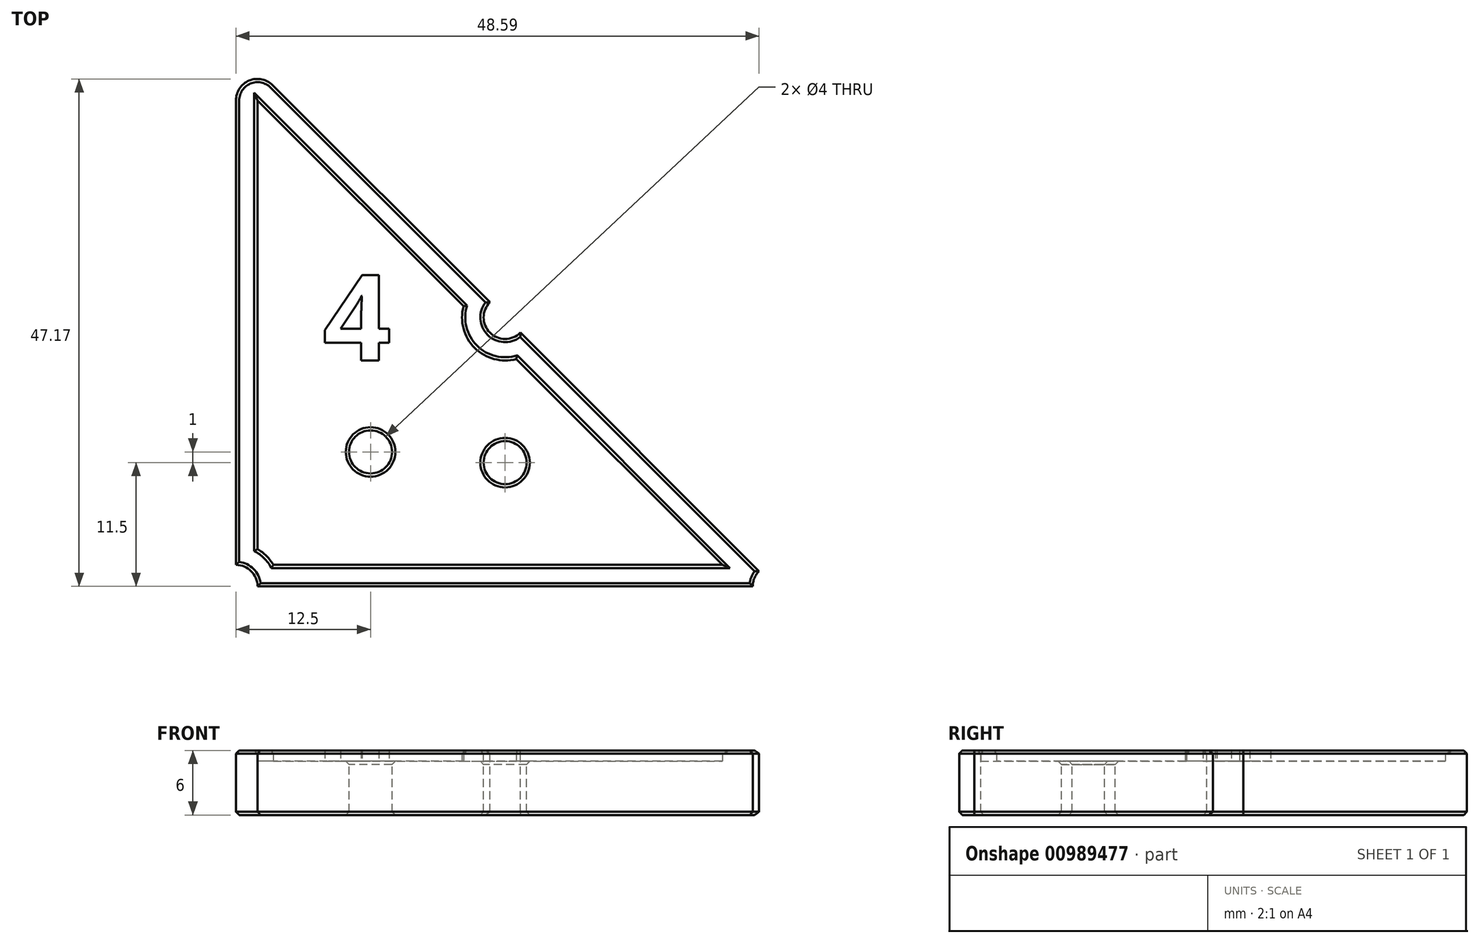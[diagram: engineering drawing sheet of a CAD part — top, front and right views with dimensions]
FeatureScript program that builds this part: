
annotation { "Feature Type Name" : "Feature", "Feature Type Description" : "" }
export const myFeature = defineFeature(function(context is Context, id is Id, definition is map)
    precondition{}
    {
        {
            var Q0;
            Q0=qCreatedBy(makeId("Top.planeOp"),FACE);
            var sketch = newSketch(context, id + "F0", { "sketchPlane" : qUnion([Q0])});
            skLineSegment(sketch, "E0", {"start": v(-25, 25) * mm, "end": v(-25, -25) * mm});
            skLineSegment(sketch, "E1", {"start": v(-25, -25) * mm, "end": v(25, -25) * mm});
            skLineSegment(sketch, "E2", {"start": v(25, -25) * mm, "end": v(-25, 25) * mm});
            skPoint(sketch, "E3", {"position": v(0, 0) * mm});
            skCircle(sketch, "E4", {"center": v(-25, -25) * mm, "radius": 2 * mm});
            skCircle(sketch, "E5", {"center": v(25, -25) * mm, "radius": 2 * mm});
            skCircle(sketch, "E6", {"center": v(0, 0) * mm, "radius": 2 * mm});
            skArc(sketch, "E7", {"start": v(-21.59, 21.59) * mm, "mid": v(-23.77, 22.02) * mm, "end": v(-25, 20.17) * mm});
            skCircle(sketch, "E8", {"center": v(-12.5, -12.5) * mm, "radius": 2 * mm});
            skLineSegment(sketch, "E9", {"start": v(0, 0) * mm, "end": v(-25, -25) * mm, "construction": true});
            skCircle(sketch, "E10", {"center": v(0, -13.5) * mm, "radius": 2 * mm});
            skLineSegment(sketch, "E11", {"start": v(0, -2) * mm, "end": v(0, -25) * mm, "construction": true});
            skPoint(sketch, "E11.startSnap0", {"position": v(0, -25) * mm});
            skLineSegment(sketch, "E12", {"start": v(-2, 2) * mm, "end": v(-2, -7.39) * mm, "construction": true});
            skLineSegment(sketch, "E13", {"start": v(-2, 0) * mm, "end": v(-25, 0) * mm, "construction": true});
            skText(sketch, "E14", { "text": "4", "fontName": "OpenSans-Bold.ttf"});
            skPoint(sketch, "E15", {"position": v(-13.5, 0) * mm});
            const initialGuessF0  = {"E14": [-0.01694, -0.004, 1, 0, 0.008]};
            skSetInitialGuess(sketch, initialGuessF0);
            skSolve(sketch);
        }
        {
            var Q0;
            Q0=makeQuery(id+"F0.imprint","IMPRINT",FACE,{"disambiguationData":[TD([[makeQuery(id+"F0.imprint","IMPRINT",EDGE,{"derivedFrom":sQuery(id+"F0.wireOp",EDGE,"E8")}),-1.0]])]});
            var Q1;
            Q1=makeQuery(id+"F0.imprint","IMPRINT",FACE,{"disambiguationData":[TD([[makeQuery(id+"F0.imprint","IMPRINT",EDGE,{"derivedFrom":sQuery(id+"F0.wireOp",EDGE,"E14.sketch_text.stroke-0")}),-1.0]])]});
            var Q2;
            Q2=makeQuery(id+"F0.imprint","IMPRINT",FACE,{"disambiguationData":[TD([[makeQuery(id+"F0.imprint","IMPRINT",EDGE,{"derivedFrom":sQuery(id+"F0.wireOp",EDGE,"E14.sketch_text.stroke-11")}),1.0]])]});
            extrude(context, id + "F1", {"entities" : qUnion([Q0, Q1, Q2]), "oppositeDirection" : true, "depth" : 5 * mm, "offsetDistance" : 25 * mm});
        }
        {
            var Q0;
            Q0=makeQuery(id+"F1.opExtrude","CAP_FACE",FACE,{"disambiguationData":[OSD([sQuery(id+"F0.wireOp",EDGE,"E0"),sQuery(id+"F0.wireOp",EDGE,"E1"),sQuery(id+"F0.wireOp",EDGE,"E2"),sQuery(id+"F0.wireOp",EDGE,"E4"),sQuery(id+"F0.wireOp",EDGE,"E5"),sQuery(id+"F0.wireOp",EDGE,"E6"),sQuery(id+"F0.wireOp",EDGE,"E7"),sQuery(id+"F0.wireOp",EDGE,"E8"),sQuery(id+"F0.wireOp",EDGE,"E10")])],"isStart":true});
            var sketch = newSketch(context, id + "F2", { "sketchPlane" : qUnion([Q0])});
            skLineSegment(sketch, "E16.0", {"start": v(20.17, -23) * mm, "end": v(1.04, -3.86) * mm});
            skArc(sketch, "E16.2", {"start": v(1.04, -3.86) * mm, "mid": v(-2.83, -2.83) * mm, "end": v(-3.86, 1.04) * mm});
            skLineSegment(sketch, "E16.3", {"start": v(-21.54, -23) * mm, "end": v(20.17, -23) * mm});
            skLineSegment(sketch, "E16.4", {"start": v(-3.86, 1.04) * mm, "end": v(-23, 20.17) * mm});
            skLineSegment(sketch, "E16.5", {"start": v(-23, 20.17) * mm, "end": v(-23, 20.17) * mm});
            skLineSegment(sketch, "E16.6", {"start": v(-23, 20.17) * mm, "end": v(-23, -21.54) * mm});
            skArc(sketch, "E16.7", {"start": v(-23, -21.54) * mm, "mid": v(-22.17, -22.17) * mm, "end": v(-21.54, -23) * mm});
            skSolve(sketch);
        }
        {
            var Q0;
            Q0=makeQuery(id+"F0.imprint","IMPRINT",FACE,{"disambiguationData":[TD([[makeQuery(id+"F0.imprint","IMPRINT",EDGE,{"derivedFrom":sQuery(id+"F0.wireOp",EDGE,"E14.sketch_text.stroke-0")}),-1.0]])]});
            var Q1;
            Q1=makeQuery(id+"F2.imprint","IMPRINT",FACE,{"disambiguationData":[TD([[makeQuery(id+"F2.imprint","IMPRINT",EDGE,{"derivedFrom":sQuery(id+"F2.wireOp",EDGE,"E16.0")}),-1.0]])]});
            extrude(context, id + "F3", {"entities" : qUnion([Q0, Q1]), "operationType" : NewBodyOperationType.ADD, "depth" : 1 * mm, "offsetDistance" : 25 * mm});
        }
        {
            var Q0;
            Q0=makeQuery(id+"F3.opExtrude","CAP_FACE",FACE,{"disambiguationData":[OSD([sQuery(id+"F0.wireOp",EDGE,"E0"),sQuery(id+"F0.wireOp",EDGE,"E1"),sQuery(id+"F0.wireOp",EDGE,"E2"),sQuery(id+"F0.wireOp",EDGE,"E4"),sQuery(id+"F0.wireOp",EDGE,"E5"),sQuery(id+"F0.wireOp",EDGE,"E6"),sQuery(id+"F0.wireOp",EDGE,"E7"),sQuery(id+"F2.wireOp",EDGE,"E16.0"),sQuery(id+"F2.wireOp",EDGE,"E16.2"),sQuery(id+"F2.wireOp",EDGE,"E16.3"),sQuery(id+"F2.wireOp",EDGE,"E16.4"),sQuery(id+"F2.wireOp",EDGE,"E16.6"),sQuery(id+"F2.wireOp",EDGE,"E16.7")])],"isStart":false});
            var Q1;
            Q1=makeQuery(id+"F1.opExtrude","CAP_EDGE",EDGE,{"disambiguationData":[OSD([sQuery(id+"F0.wireOp",EDGE,"E8")])],"isStart":true});
            var Q2;
            Q2=makeQuery(id+"F1.opExtrude","CAP_EDGE",EDGE,{"disambiguationData":[OSD([sQuery(id+"F0.wireOp",EDGE,"E10")])],"isStart":true});
            var Q3;
            Q3=makeQuery(id+"F1.opExtrude","CAP_FACE",FACE,{"disambiguationData":[OSD([sQuery(id+"F0.wireOp",EDGE,"E0"),sQuery(id+"F0.wireOp",EDGE,"E1"),sQuery(id+"F0.wireOp",EDGE,"E2"),sQuery(id+"F0.wireOp",EDGE,"E4"),sQuery(id+"F0.wireOp",EDGE,"E5"),sQuery(id+"F0.wireOp",EDGE,"E6"),sQuery(id+"F0.wireOp",EDGE,"E7"),sQuery(id+"F0.wireOp",EDGE,"E8"),sQuery(id+"F0.wireOp",EDGE,"E10")])],"isStart":false});
            chamfer(context, id + "F4", {"entities" : qUnion([Q0, Q1, Q2, Q3]), "width" : 0.3 * mm, "tangentPropagation" : true});
        }
    });
